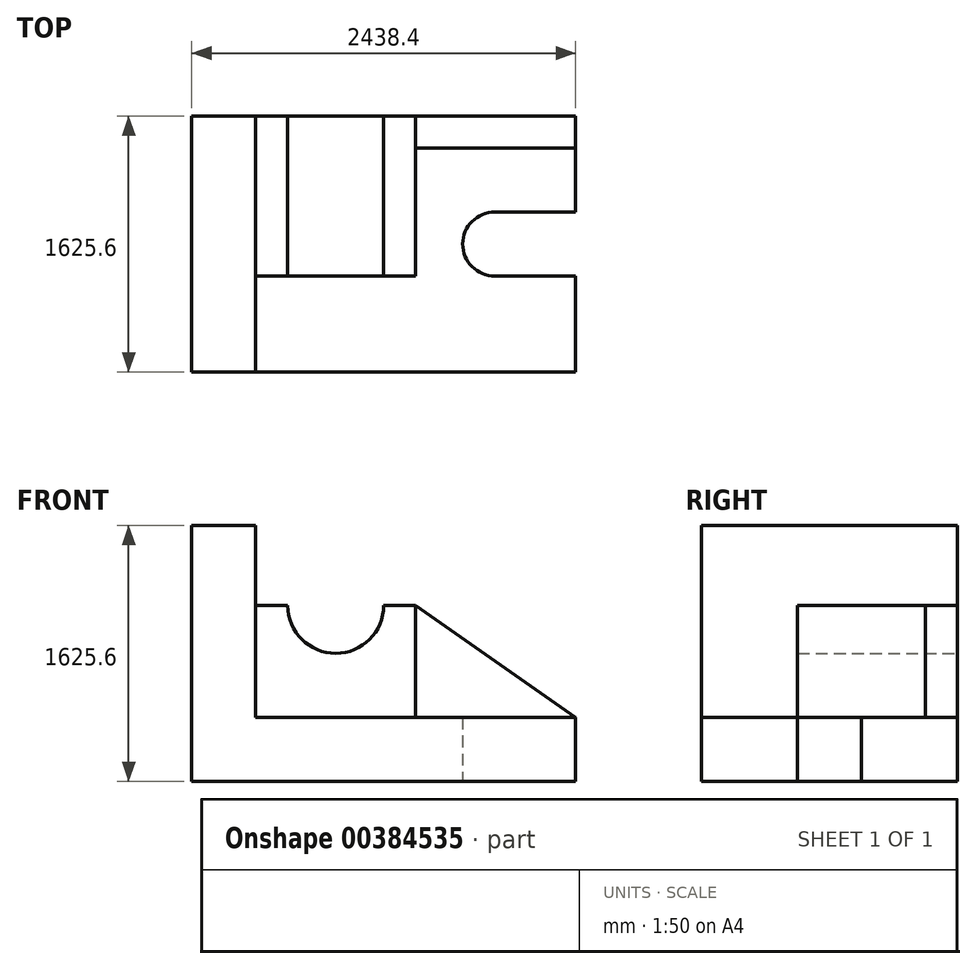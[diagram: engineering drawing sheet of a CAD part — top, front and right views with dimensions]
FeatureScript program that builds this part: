
annotation { "Feature Type Name" : "Feature", "Feature Type Description" : "" }
export const myFeature = defineFeature(function(context is Context, id is Id, definition is map)
    precondition{}
    {
        {
            var Q0;
            Q0=qCreatedBy(makeId("Front.planeOp"),FACE);
            var sketch = newSketch(context, id + "F0", { "sketchPlane" : qUnion([Q0])});
            skLineSegment(sketch, "E0", {"start": v(0, 0) * mm, "end": v(98.23, 0) * mm});
            skLineSegment(sketch, "E1", {"start": v(0, 0) * mm, "end": v(2438.4, 0) * mm});
            skLineSegment(sketch, "E2", {"start": v(2438.4, 0) * mm, "end": v(2438.4, 406.4) * mm});
            skLineSegment(sketch, "E3", {"start": v(2438.4, 406.4) * mm, "end": v(406.4, 406.4) * mm});
            skLineSegment(sketch, "E4", {"start": v(406.4, 406.4) * mm, "end": v(406.4, 1625.6) * mm});
            skLineSegment(sketch, "E5", {"start": v(406.4, 1625.6) * mm, "end": v(0, 1625.6) * mm});
            skLineSegment(sketch, "E6", {"start": v(0, 1625.6) * mm, "end": v(0, 0) * mm});
            skSolve(sketch);
        }
        {
            var Q0;
            Q0=qCreatedBy(makeId("Top.planeOp"),FACE);
            var sketch = newSketch(context, id + "F1", { "sketchPlane" : qUnion([Q0])});
            skLineSegment(sketch, "E7", {"start": v(2457.33, 1016) * mm, "end": v(1923.93, 1016) * mm});
            skPoint(sketch, "E8", {"position": v(1923.93, 812.8) * mm});
            skArc(sketch, "E9", {"start": v(1923.93, 1016) * mm, "mid": v(1720.73, 812.8) * mm, "end": v(1923.93, 609.6) * mm});
            skLineSegment(sketch, "E10", {"start": v(1923.93, 609.6) * mm, "end": v(2457.33, 609.6) * mm});
            skLineSegment(sketch, "E11", {"start": v(2457.33, 609.6) * mm, "end": v(2457.33, 1016) * mm});
            skSolve(sketch);
        }
        {
            var Q0;
            {var subQ0=sQuery(id+"F0.wireOp",EDGE,"E2");Q0=makeQuery(id+"F0.imprint","IMPRINT",FACE,{"disambiguationData":[TD([[makeQuery(id+"F0.imprint","IMPRINT",EDGE,{"derivedFrom":subQ0}),1.0]])]});}
            extrude(context, id + "F2", {"entities" : qUnion([Q0]), "oppositeDirection" : true, "depth" : 1625.6 * mm});
        }
        {
            var Q0;
            Q0=makeQuery(id+"F1.imprint","IMPRINT",FACE,{"disambiguationData":[TD([[makeQuery(id+"F1.imprint","IMPRINT",EDGE,{"derivedFrom":sQuery(id+"F1.wireOp",EDGE,"E7")}),1.0]])]});
            extrude(context, id + "F3", {"entities" : qUnion([Q0]), "operationType" : NewBodyOperationType.REMOVE, "endBound" : BoundingType.THROUGH_ALL, "depth" : 25.4 * mm});
        }
        {
            var Q0;
            Q0=makeQuery(id+"F2.opExtrude","SWEPT_FACE",FACE,{"disambiguationData":[OSD([sQuery(id+"F0.wireOp",EDGE,"E6")])]});
            var sketch = newSketch(context, id + "F4", { "sketchPlane" : qUnion([Q0])});
            skLineSegment(sketch, "E12", {"start": v(-633.55, 1655.54) * mm, "end": v(198.59, 615.37) * mm});
            skPoint(sketch, "E13", {"position": v(0, 863.6) * mm});
            skPoint(sketch, "E14", {"position": v(-609.6, 1625.6) * mm});
            skLineSegment(sketch, "E15", {"start": v(-609.6, 1625.6) * mm, "end": v(0, 863.6) * mm});
            skLineSegment(sketch, "E16", {"start": v(-633.55, 1655.54) * mm, "end": v(308.26, 1655.54) * mm});
            skLineSegment(sketch, "E17", {"start": v(308.26, 1655.54) * mm, "end": v(198.59, 615.37) * mm});
            skSolve(sketch);
        }
        {
            var Q0;
            {var subQ1=sQuery(id+"F4.wireOp",EDGE,"E16");Q0=makeQuery(id+"F4.imprint","IMPRINT",FACE,{"disambiguationData":[TD([[makeQuery(id+"F4.imprint","IMPRINT",EDGE,{"derivedFrom":subQ1}),-1.0]])]});}
            var Q1;
            {var subQ0=sQuery(id+"F4.wireOp",EDGE,"E15");Q1=makeQuery(id+"F4.imprint","IMPRINT",FACE,{"disambiguationData":[TD([[makeQuery(id+"F4.imprint","IMPRINT",EDGE,{"derivedFrom":subQ0}),1.0]])]});}
            extrude(context, id + "F5", {"entities" : qUnion([Q0, Q1]), "operationType" : NewBodyOperationType.REMOVE, "endBound" : BoundingType.THROUGH_ALL, "oppositeDirection" : true, "depth" : 25.4 * mm});
        }
        {
            var Q0;
            Q0=makeQuery(id+"F2.opExtrude","CAP_FACE",FACE,{"disambiguationData":[OSD([sQuery(id+"F0.wireOp",EDGE,"E1"),sQuery(id+"F0.wireOp",EDGE,"E2"),sQuery(id+"F0.wireOp",EDGE,"E3"),sQuery(id+"F0.wireOp",EDGE,"E4"),sQuery(id+"F0.wireOp",EDGE,"E5"),sQuery(id+"F0.wireOp",EDGE,"E6")])],"isStart":false});
            var sketch = newSketch(context, id + "F6", { "sketchPlane" : qUnion([Q0])});
            skLineSegment(sketch, "E18", {"start": v(-406.4, 1117.6) * mm, "end": v(-609.6, 1117.6) * mm});
            skLineSegment(sketch, "E19", {"start": v(-1422.4, 1117.6) * mm, "end": v(-1422.4, 406.4) * mm});
            skLineSegment(sketch, "E20", {"start": v(-1422.4, 406.4) * mm, "end": v(-406.4, 406.4) * mm});
            skLineSegment(sketch, "E21", {"start": v(-406.4, 406.4) * mm, "end": v(-406.4, 1117.6) * mm});
            skLineSegment(sketch, "E22", {"start": v(-1219.2, 1117.6) * mm, "end": v(-1219.2, 1117.6) * mm});
            skLineSegment(sketch, "E23", {"start": v(-1422.4, 1117.6) * mm, "end": v(-1219.2, 1117.6) * mm});
            skArc(sketch, "E24", {"start": v(-1219.2, 1117.6) * mm, "mid": v(-914.4, 813.5) * mm, "end": v(-609.6, 1117.6) * mm});
            skSolve(sketch);
        }
        {
            var Q0;
            Q0=makeQuery(id+"F6.imprint","IMPRINT",FACE,{"disambiguationData":[TD([[makeQuery(id+"F6.imprint","IMPRINT",EDGE,{"derivedFrom":sQuery(id+"F6.wireOp",EDGE,"E18")}),1.0]])]});
            extrude(context, id + "F7", {"entities" : qUnion([Q0]), "oppositeDirection" : true, "depth" : 1016 * mm});
        }
        {
            var Q0;
            Q0=makeQuery(id+"F7.opExtrude","CAP_FACE",FACE,{"disambiguationData":[OSD([sQuery(id+"F6.wireOp",EDGE,"E18"),sQuery(id+"F6.wireOp",EDGE,"E19"),sQuery(id+"F6.wireOp",EDGE,"E20"),sQuery(id+"F6.wireOp",EDGE,"E21"),sQuery(id+"F6.wireOp",EDGE,"E23"),sQuery(id+"F6.wireOp",EDGE,"E24")])],"isStart":true});
            var sketch = newSketch(context, id + "F8", { "sketchPlane" : qUnion([Q0])});
            skLineSegment(sketch, "E25", {"start": v(-1422.4, 1117.6) * mm, "end": v(-1422.4, 406.4) * mm});
            skLineSegment(sketch, "E26", {"start": v(-1422.4, 406.4) * mm, "end": v(-2438.4, 406.4) * mm});
            skLineSegment(sketch, "E27", {"start": v(-2438.4, 406.4) * mm, "end": v(-1422.4, 1117.6) * mm});
            skSolve(sketch);
        }
        {
            var Q0;
            Q0=makeQuery(id+"F8.imprint","IMPRINT",FACE,{"disambiguationData":[TD([[makeQuery(id+"F8.imprint","IMPRINT",EDGE,{"derivedFrom":sQuery(id+"F8.wireOp",EDGE,"E25")}),-1.0]])]});
            extrude(context, id + "F9", {"entities" : qUnion([Q0]), "oppositeDirection" : true, "depth" : 203.2 * mm});
        }
    });
